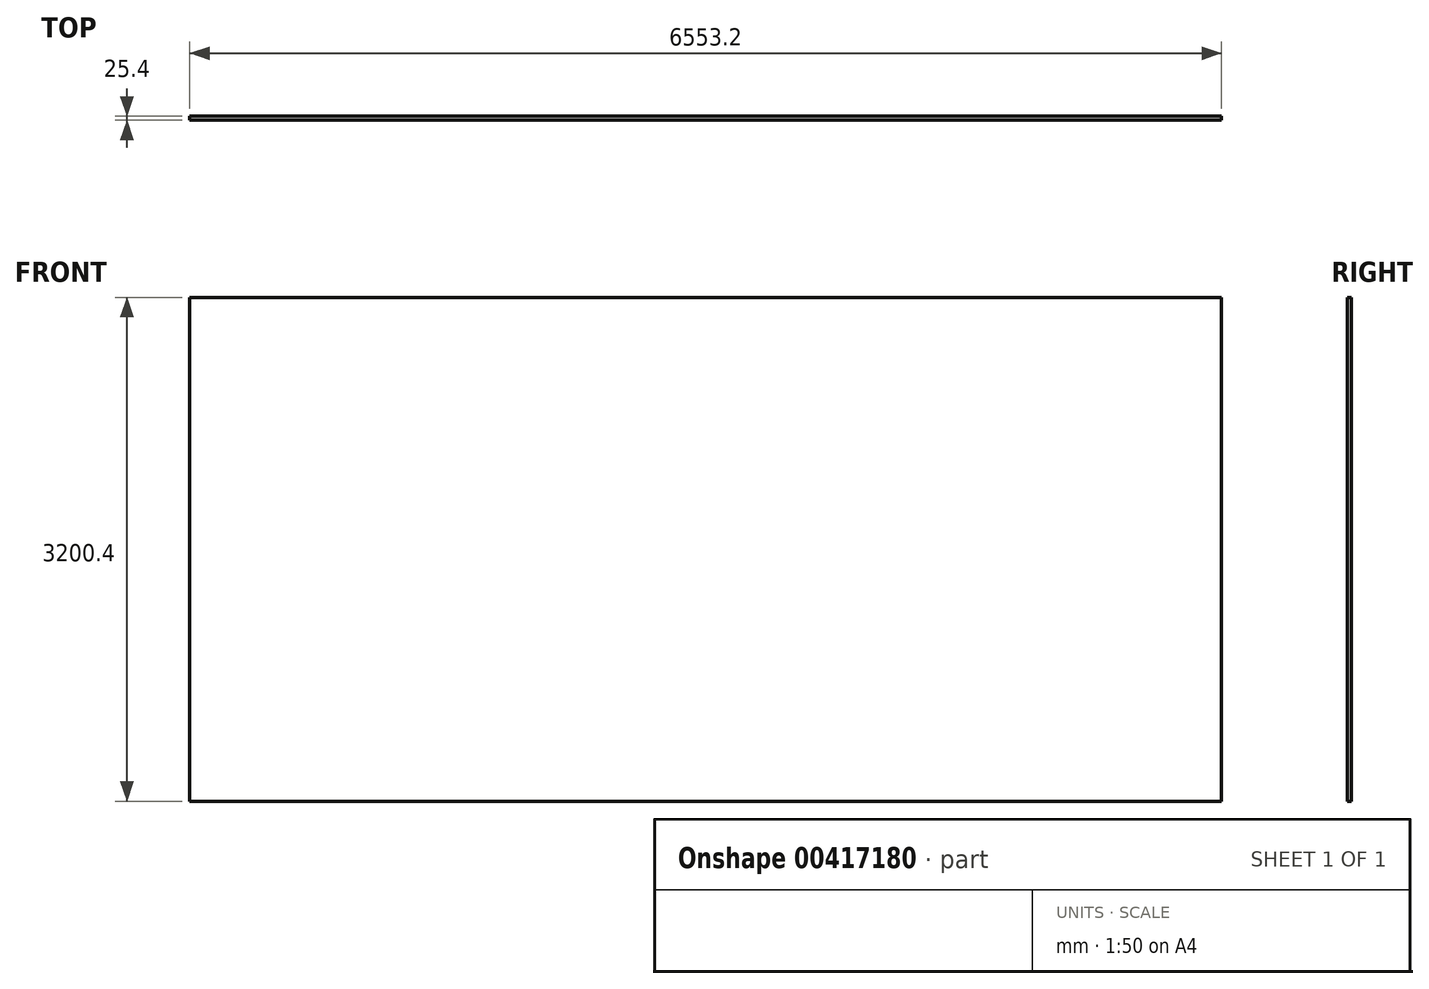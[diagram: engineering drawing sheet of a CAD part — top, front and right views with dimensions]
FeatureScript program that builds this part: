
annotation { "Feature Type Name" : "Feature", "Feature Type Description" : "" }
export const myFeature = defineFeature(function(context is Context, id is Id, definition is map)
    precondition{}
    {
        {
            var Q0;
            Q0=qCreatedBy(makeId("Front.planeOp"),FACE);
            var sketch = newSketch(context, id + "F0", { "sketchPlane" : qUnion([Q0])});
            skLineSegment(sketch, "E0.bottom", {"start": v(0, 0) * mm, "end": v(6553.2, 0) * mm});
            skLineSegment(sketch, "E0.top", {"start": v(0, 3200.4) * mm, "end": v(6553.2, 3200.4) * mm});
            skLineSegment(sketch, "E0.left", {"start": v(0, 0) * mm, "end": v(0, 3200.4) * mm});
            skLineSegment(sketch, "E0.right", {"start": v(6553.2, 0) * mm, "end": v(6553.2, 3200.4) * mm});
            skSolve(sketch);
        }
        {
            var Q0;
            Q0=makeQuery(id+"F0.imprint","IMPRINT",FACE,{"disambiguationData":[TD([[makeQuery(id+"F0.imprint","IMPRINT",EDGE,{"derivedFrom":sQuery(id+"F0.wireOp",EDGE,"E0.bottom")}),1.0]])]});
            extrude(context, id + "F1", {"entities" : qUnion([Q0]), "oppositeDirection" : true, "depth" : 25.4 * mm});
        }
    });
